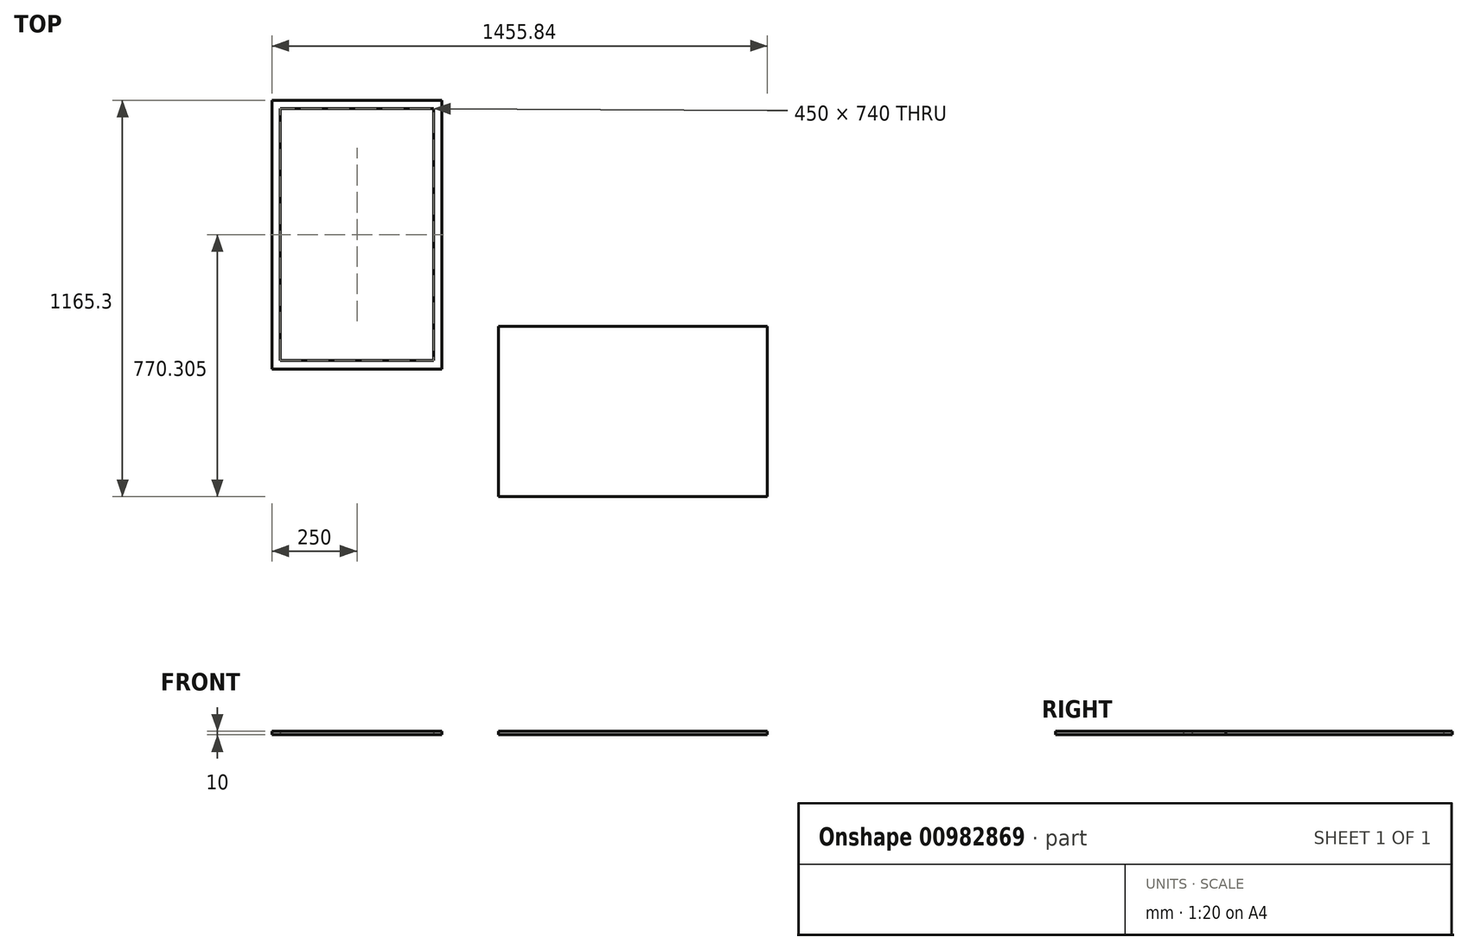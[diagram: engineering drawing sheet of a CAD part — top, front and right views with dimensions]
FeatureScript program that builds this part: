
annotation { "Feature Type Name" : "Feature", "Feature Type Description" : "" }
export const myFeature = defineFeature(function(context is Context, id is Id, definition is map)
    precondition{}
    {
        {
            var Q0;
            Q0=qCreatedBy(makeId("Top.planeOp"),FACE);
            var sketch = newSketch(context, id + "F0", { "sketchPlane" : qUnion([Q0])});
            skLineSegment(sketch, "E0.left", {"start": v(-1182.9, 953.87) * mm, "end": v(-1182.9, 653.87) * mm});
            skLineSegment(sketch, "E1.bottom", {"start": v(-1207.9, 1248.87) * mm, "end": v(-1182.9, 1248.87) * mm});
            skLineSegment(sketch, "E1.top", {"start": v(-1207.9, 458.87) * mm, "end": v(-1182.9, 458.87) * mm});
            skLineSegment(sketch, "E1.left", {"start": v(-1207.9, 1248.87) * mm, "end": v(-1207.9, 458.87) * mm});
            skLineSegment(sketch, "E1.right", {"start": v(-1182.9, 1248.87) * mm, "end": v(-1182.9, 458.87) * mm});
            skLineSegment(sketch, "E2.left", {"start": v(-1182.9, 458.87) * mm, "end": v(-1182.9, 483.87) * mm});
            skLineSegment(sketch, "E3.left", {"start": v(-1182.9, 1248.87) * mm, "end": v(-1182.9, 1223.87) * mm});
            skLineSegment(sketch, "E4", {"start": v(-732.9, 458.87) * mm, "end": v(-732.9, 1248.87) * mm});
            skLineSegment(sketch, "E5", {"start": v(-707.9, 1248.87) * mm, "end": v(-707.9, 458.87) * mm});
            skLineSegment(sketch, "E6", {"start": v(-1182.9, 1223.87) * mm, "end": v(-707.9, 1223.87) * mm});
            skLineSegment(sketch, "E7", {"start": v(-1182.9, 483.87) * mm, "end": v(-707.9, 483.87) * mm});
            skLineSegment(sketch, "E8", {"start": v(-1182.9, 458.87) * mm, "end": v(-707.9, 458.87) * mm});
            skLineSegment(sketch, "E9", {"start": v(-1182.9, 1248.87) * mm, "end": v(-707.9, 1248.87) * mm});
            skLineSegment(sketch, "E10", {"start": v(-1182.9, 483.87) * mm, "end": v(-1207.9, 483.87) * mm});
            skLineSegment(sketch, "E11.bottom", {"start": v(-347.06, 108.57) * mm, "end": v(-47.06, 108.57) * mm});
            skLineSegment(sketch, "E12", {"start": v(-347.06, 108.57) * mm, "end": v(-542.06, 108.57) * mm});
            skLineSegment(sketch, "E13", {"start": v(-542.06, 108.57) * mm, "end": v(-542.06, 83.57) * mm});
            skLineSegment(sketch, "E14", {"start": v(-542.06, 83.57) * mm, "end": v(247.94, 83.57) * mm});
            skLineSegment(sketch, "E15", {"start": v(247.94, 83.57) * mm, "end": v(247.94, 108.57) * mm});
            skLineSegment(sketch, "E16", {"start": v(247.94, 108.57) * mm, "end": v(-47.06, 108.57) * mm});
            skLineSegment(sketch, "E17.bottom", {"start": v(-542.06, 108.57) * mm, "end": v(-517.06, 108.57) * mm});
            skLineSegment(sketch, "E18.bottom", {"start": v(247.94, 108.57) * mm, "end": v(222.94, 108.57) * mm});
            skLineSegment(sketch, "E19.top", {"start": v(-309.56, 83.57) * mm, "end": v(-284.56, 83.57) * mm});
            skLineSegment(sketch, "E20.top", {"start": v(-9.56, 83.57) * mm, "end": v(15.44, 83.57) * mm});
            skLineSegment(sketch, "E21", {"start": v(-542.06, 583.57) * mm, "end": v(247.94, 583.57) * mm});
            skLineSegment(sketch, "E22", {"start": v(-542.06, 558.57) * mm, "end": v(247.94, 558.57) * mm});
            skLineSegment(sketch, "E23", {"start": v(-542.06, 583.57) * mm, "end": v(-542.06, 83.57) * mm});
            skLineSegment(sketch, "E24", {"start": v(247.94, 83.57) * mm, "end": v(247.94, 583.57) * mm});
            skLineSegment(sketch, "E25", {"start": v(-517.06, 108.57) * mm, "end": v(-517.06, 583.57) * mm});
            skLineSegment(sketch, "E26", {"start": v(222.94, 108.57) * mm, "end": v(222.94, 583.57) * mm});
            skLineSegment(sketch, "E27", {"start": v(-517.06, 108.57) * mm, "end": v(-517.06, 83.57) * mm});
            skSolve(sketch);
        }
        {
            var Q0;
            Q0 = qSketchRegion(id + "F0", true);
            var Q1;
            {var subQ1=sQuery(id+"F0.wireOp",EDGE,"E1.right");var subQ9=makeQuery(id+"F0.imprint","IMPRINT",VERTEX,{"disambiguationData":[OD(0.0)],"derivedFrom":subQ1});Q1=makeQuery(id+"F0.imprint","IMPRINT",FACE,{"disambiguationData":[TD([[makeQuery(id+"F0.imprint","IMPRINT",EDGE,{"disambiguationData":[TD([[subQ9,-1.0]])],"derivedFrom":subQ1}),1.0]])]});}
            var Q2;
            Q2=makeQuery(id+"F0.imprint","IMPRINT",FACE,{"disambiguationData":[TD([[makeQuery(id+"F0.imprint","IMPRINT",EDGE,{"derivedFrom":sQuery(id+"F0.wireOp",EDGE,"d3ba89f9-839a-49ad-9ddb-324f2d2f1175.bottom")}),1.0]])]});
            var Q3;
            Q3=makeQuery(id+"F0.imprint","IMPRINT",FACE,{"disambiguationData":[TD([[makeQuery(id+"F0.imprint","IMPRINT",EDGE,{"derivedFrom":sQuery(id+"F0.wireOp",EDGE,"E11.bottom")}),1.0]])]});
            extrude(context, id + "F1", {"entities" : qUnion([Q0, Q1, Q2, Q3]), "depth" : 10 * mm, "offsetDistance" : 25 * mm});
        }
    });
